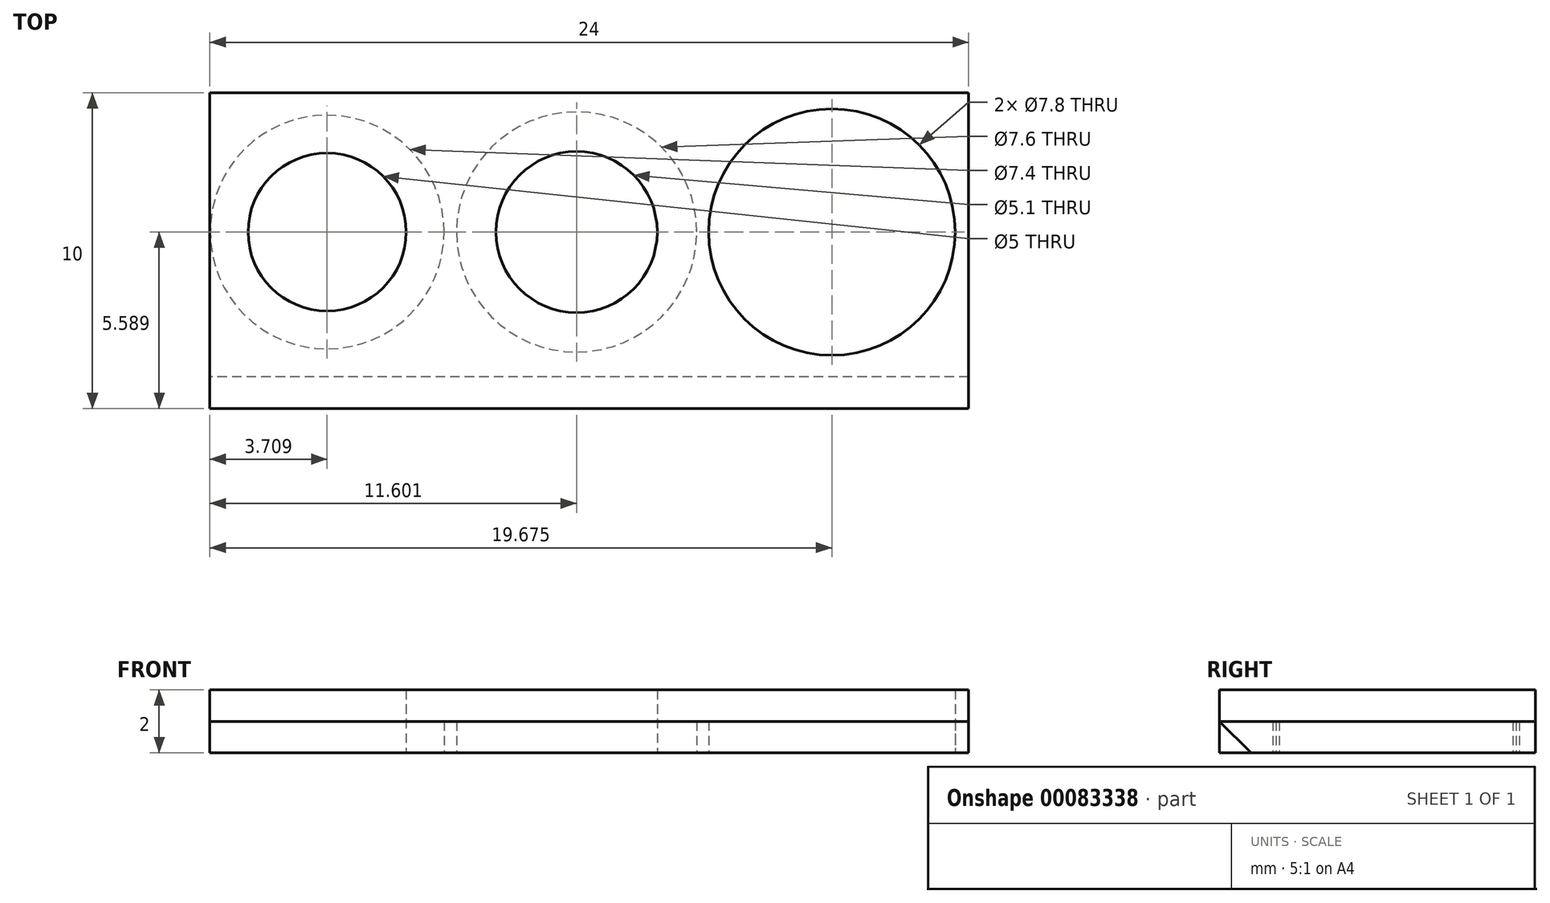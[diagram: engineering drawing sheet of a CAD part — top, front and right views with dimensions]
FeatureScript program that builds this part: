
annotation { "Feature Type Name" : "Feature", "Feature Type Description" : "" }
export const myFeature = defineFeature(function(context is Context, id is Id, definition is map)
    precondition{}
    {
        {
            var Q0;
            Q0=qCreatedBy(makeId("Top.planeOp"),FACE);
            var sketch = newSketch(context, id + "F0", { "sketchPlane" : qUnion([Q0])});
            skLineSegment(sketch, "E0.bottom", {"start": v(-24.15, 7.11) * mm, "end": v(-0.15, 7.11) * mm});
            skLineSegment(sketch, "E0.top", {"start": v(-24.15, -2.89) * mm, "end": v(-0.15, -2.89) * mm});
            skLineSegment(sketch, "E0.left", {"start": v(-24.15, 7.11) * mm, "end": v(-24.15, -2.89) * mm});
            skLineSegment(sketch, "E0.right", {"start": v(-0.15, 7.11) * mm, "end": v(-0.15, -2.89) * mm});
            skLineSegment(sketch, "E1", {"start": v(-24.15, 2.7) * mm, "end": v(-0.15, 2.7) * mm});
            skLineSegment(sketch, "E2", {"start": v(-0.15, 2.7) * mm, "end": v(-0.28, 2.4) * mm});
            skCircle(sketch, "E3", {"center": v(-20.44, 2.7) * mm, "radius": 2.5 * mm});
            skCircle(sketch, "E4", {"center": v(-20.44, 2.7) * mm, "radius": 3.7 * mm});
            skCircle(sketch, "E5", {"center": v(-12.55, 2.7) * mm, "radius": 2.55 * mm});
            skCircle(sketch, "E6", {"center": v(-12.55, 2.7) * mm, "radius": 3.8 * mm});
            skCircle(sketch, "E7", {"center": v(-4.47, 2.7) * mm, "radius": 2.6 * mm});
            skCircle(sketch, "E8", {"center": v(-4.47, 2.7) * mm, "radius": 3.9 * mm});
            skSolve(sketch);
        }
        {
            var Q0;
            {var subQ0=sQuery(id+"F0.wireOp",EDGE,"E4");var subQ1=sQuery(id+"F0.wireOp",EDGE,"E1");var subQ2=makeQuery(id+"F0.imprint","INTERSECT",VERTEX,{"disambiguationData":[OD(0.0)],"derivedFrom":[subQ1,subQ0]});Q0=makeQuery(id+"F0.imprint","IMPRINT",FACE,{"disambiguationData":[TD([[makeQuery(id+"F0.imprint","IMPRINT",EDGE,{"disambiguationData":[TD([[subQ2,-1.0]])],"derivedFrom":subQ1}),1.0]])]});}
            var Q1;
            {var subQ0=sQuery(id+"F0.wireOp",EDGE,"E4");var subQ1=sQuery(id+"F0.wireOp",EDGE,"E1");var subQ2=makeQuery(id+"F0.imprint","INTERSECT",VERTEX,{"disambiguationData":[OD(0.0)],"derivedFrom":[subQ1,subQ0]});Q1=makeQuery(id+"F0.imprint","IMPRINT",FACE,{"disambiguationData":[TD([[makeQuery(id+"F0.imprint","IMPRINT",EDGE,{"disambiguationData":[TD([[subQ2,-1.0]])],"derivedFrom":subQ1}),-1.0]])]});}
            var Q2;
            {var subQ0=sQuery(id+"F0.wireOp",EDGE,"E6");var subQ1=sQuery(id+"F0.wireOp",EDGE,"E1");var subQ2=makeQuery(id+"F0.imprint","INTERSECT",VERTEX,{"disambiguationData":[OD(0.0)],"derivedFrom":[subQ1,subQ0]});Q2=makeQuery(id+"F0.imprint","IMPRINT",FACE,{"disambiguationData":[TD([[makeQuery(id+"F0.imprint","IMPRINT",EDGE,{"disambiguationData":[TD([[subQ2,-1.0]])],"derivedFrom":subQ1}),1.0]])]});}
            var Q3;
            {var subQ0=sQuery(id+"F0.wireOp",EDGE,"E6");var subQ1=sQuery(id+"F0.wireOp",EDGE,"E1");var subQ2=makeQuery(id+"F0.imprint","INTERSECT",VERTEX,{"disambiguationData":[OD(0.0)],"derivedFrom":[subQ1,subQ0]});Q3=makeQuery(id+"F0.imprint","IMPRINT",FACE,{"disambiguationData":[TD([[makeQuery(id+"F0.imprint","IMPRINT",EDGE,{"disambiguationData":[TD([[subQ2,-1.0]])],"derivedFrom":subQ1}),-1.0]])]});}
            var Q4;
            {var subQ0=sQuery(id+"F0.wireOp",EDGE,"E8");var subQ1=sQuery(id+"F0.wireOp",EDGE,"E1");var subQ2=makeQuery(id+"F0.imprint","INTERSECT",VERTEX,{"disambiguationData":[OD(0.0)],"derivedFrom":[subQ1,subQ0]});Q4=makeQuery(id+"F0.imprint","IMPRINT",FACE,{"disambiguationData":[TD([[makeQuery(id+"F0.imprint","IMPRINT",EDGE,{"disambiguationData":[TD([[subQ2,-1.0]])],"derivedFrom":subQ1}),1.0]])]});}
            var Q5;
            {var subQ0=sQuery(id+"F0.wireOp",EDGE,"E8");var subQ1=sQuery(id+"F0.wireOp",EDGE,"E1");var subQ2=makeQuery(id+"F0.imprint","INTERSECT",VERTEX,{"disambiguationData":[OD(0.0)],"derivedFrom":[subQ1,subQ0]});Q5=makeQuery(id+"F0.imprint","IMPRINT",FACE,{"disambiguationData":[TD([[makeQuery(id+"F0.imprint","IMPRINT",EDGE,{"disambiguationData":[TD([[subQ2,-1.0]])],"derivedFrom":subQ1}),-1.0]])]});}
            extrude(context, id + "F1", {"entities" : qUnion([Q0, Q1, Q2, Q3, Q4, Q5]), "depth" : 2 * mm});
        }
        {
            var Q0;
            {var subQ6=sQuery(id+"F0.wireOp",EDGE,"E0.bottom");Q0=makeQuery(id+"F0.imprint","IMPRINT",FACE,{"disambiguationData":[TD([[makeQuery(id+"F0.imprint","IMPRINT",EDGE,{"derivedFrom":subQ6}),-1.0]])]});}
            var Q1;
            {var subQ6=sQuery(id+"F0.wireOp",EDGE,"E0.top");Q1=makeQuery(id+"F0.imprint","IMPRINT",FACE,{"disambiguationData":[TD([[makeQuery(id+"F0.imprint","IMPRINT",EDGE,{"derivedFrom":subQ6}),1.0]])]});}
            extrude(context, id + "F2", {"entities" : qUnion([Q0, Q1]), "depth" : 1 * mm});
        }
        {
            var Q0;
            Q0=makeQuery(id+"F2.opExtrude","CAP_EDGE",EDGE,{"disambiguationData":[OSD([sQuery(id+"F0.wireOp",EDGE,"E0.top")])],"isStart":true});
            chamfer(context, id + "F3", {"entities" : qUnion([Q0]), "width" : 1 * mm, "tangentPropagation" : true});
        }
    });
